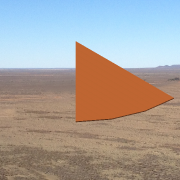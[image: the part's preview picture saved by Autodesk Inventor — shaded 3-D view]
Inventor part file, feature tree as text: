
AUTODESK INVENTOR PART (.ipt)
format: ipt  version: 2013 SP2 (Build 170200200, 200)  size: 131,584 bytes
history: native  units: in
note: dims shown in document units (in); Inventor stores cm internally (conversion verified against a paired STEP export)
features: extrude x1, sketch x1
ambient origin geometry x8: Origin, YZ Plane, XZ Plane, XY Plane, X Axis, Y Axis, Z Axis, Center Point
bodies: Solid1 (feature_tree)
feature tree (2):
  extrude  "Extrusion1"  Depth=192.0in
  sketch  "Sketch1"  dims[d0=192.0in d8=192.0in d9=15.0deg d10=192.0in d11=30.0deg d12=192.0in d13=45.0deg d14=130.32in d15=60.0deg d18=122.52in d19=105.0deg d20=1.5in d21=0.0in]
